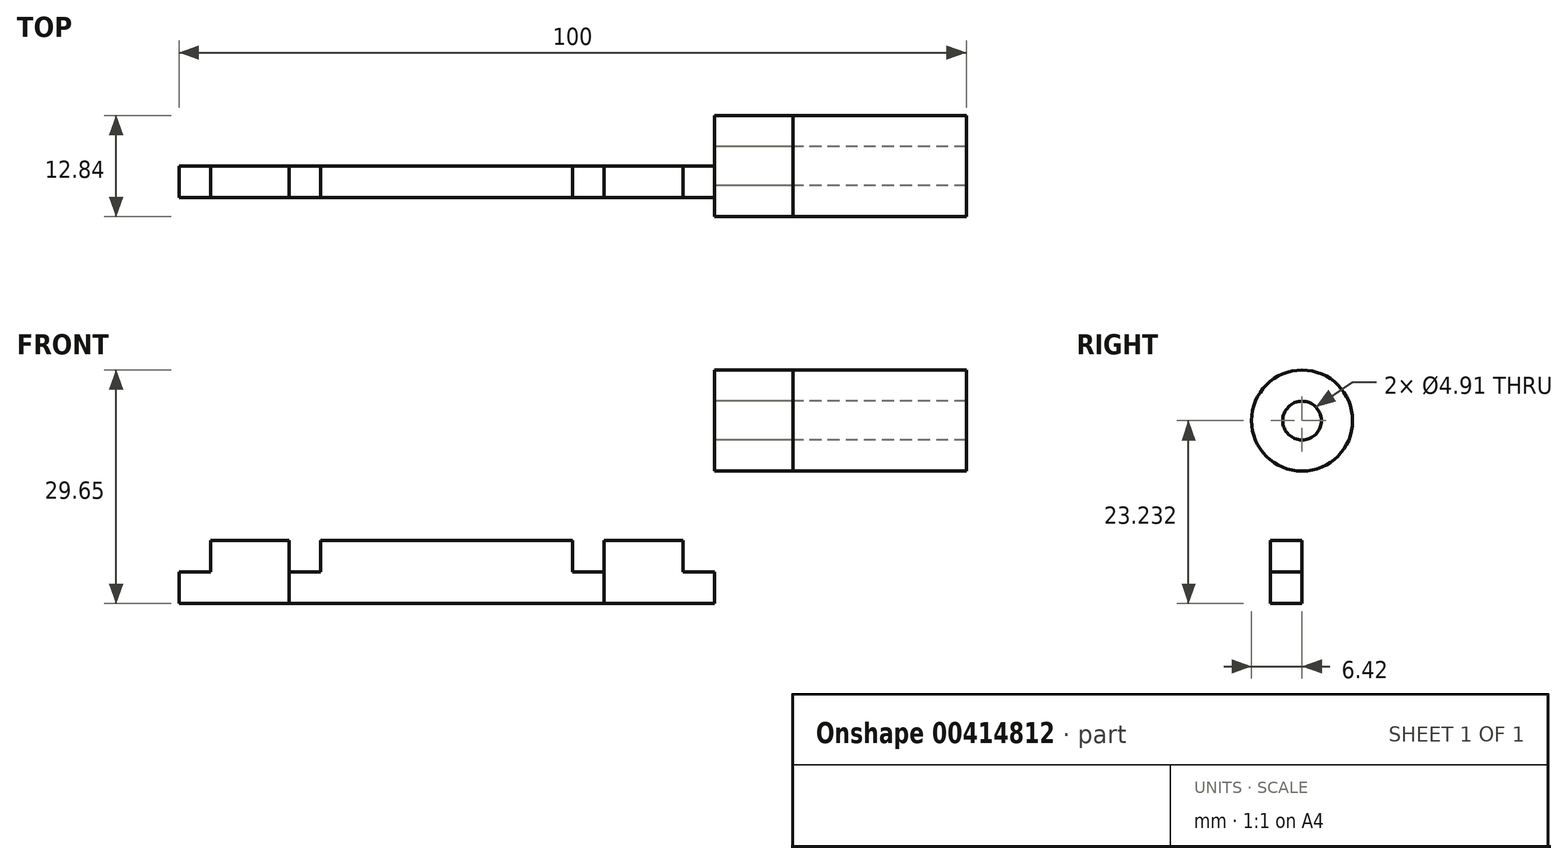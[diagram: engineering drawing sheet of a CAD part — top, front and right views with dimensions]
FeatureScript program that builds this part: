
annotation { "Feature Type Name" : "Feature", "Feature Type Description" : "" }
export const myFeature = defineFeature(function(context is Context, id is Id, definition is map)
    precondition{}
    {
        {
            var Q0;
            Q0=qCreatedBy(makeId("Front.planeOp"),FACE);
            var sketch = newSketch(context, id + "F0", { "sketchPlane" : qUnion([Q0])});
            skLineSegment(sketch, "E0", {"start": v(0, 0) * mm, "end": v(-68, 0) * mm});
            skLineSegment(sketch, "E1", {"start": v(-68, 0) * mm, "end": v(-68, 4) * mm});
            skLineSegment(sketch, "E2", {"start": v(-68, 4) * mm, "end": v(-64, 4) * mm});
            skLineSegment(sketch, "E3", {"start": v(-64, 4) * mm, "end": v(-64, 8) * mm});
            skLineSegment(sketch, "E4", {"start": v(-64, 8) * mm, "end": v(-54, 8) * mm});
            skLineSegment(sketch, "E5", {"start": v(-54, 8) * mm, "end": v(-54, 4) * mm});
            skLineSegment(sketch, "E6", {"start": v(-54, 4) * mm, "end": v(-50, 4) * mm});
            skLineSegment(sketch, "E7", {"start": v(-50, 4) * mm, "end": v(-50, 8) * mm});
            skLineSegment(sketch, "E8", {"start": v(-50, 8) * mm, "end": v(-18, 8) * mm});
            skLineSegment(sketch, "E9", {"start": v(-18, 8) * mm, "end": v(-18, 4) * mm});
            skLineSegment(sketch, "E10", {"start": v(-18, 4) * mm, "end": v(-14, 4) * mm});
            skLineSegment(sketch, "E11", {"start": v(-14, 4) * mm, "end": v(-14, 8) * mm});
            skLineSegment(sketch, "E12", {"start": v(-14, 8) * mm, "end": v(-4, 8) * mm});
            skLineSegment(sketch, "E13", {"start": v(-4, 8) * mm, "end": v(-4, 4) * mm});
            skLineSegment(sketch, "E14", {"start": v(-4, 4) * mm, "end": v(0, 4) * mm});
            skLineSegment(sketch, "E15", {"start": v(0, 4) * mm, "end": v(0, 0) * mm});
            skLineSegment(sketch, "E16", {"start": v(-54, 4) * mm, "end": v(-54, 0) * mm});
            skLineSegment(sketch, "E17", {"start": v(-14, 4) * mm, "end": v(-14, 0) * mm});
            skSolve(sketch);
        }
        {
            var Q0;
            Q0 = qSketchRegion(id + "F0", true);
            extrude(context, id + "F1", {"entities" : qUnion([Q0]), "depth" : 4 * mm});
        }
        {
            var Q0;
            Q0=makeQuery(id+"F0.imprint","IMPRINT",FACE,{"disambiguationData":[TD([[makeQuery(id+"F0.imprint","IMPRINT",EDGE,{"derivedFrom":sQuery(id+"F0.wireOp",EDGE,"E6")}),-1.0]])]});
            extrude(context, id + "F2", {"entities" : qUnion([Q0]), "depth" : 4 * mm});
        }
        {
            var Q0;
            Q0=qCreatedBy(makeId("Right.planeOp"),FACE);
            var sketch = newSketch(context, id + "F3", { "sketchPlane" : qUnion([Q0])});
            skCircle(sketch, "E18", {"center": v(0, 23.23) * mm, "radius": 2.46 * mm});
            skCircle(sketch, "E19", {"center": v(0, 23.23) * mm, "radius": 6.42 * mm});
            skSolve(sketch);
        }
        {
            var Q0;
            Q0 = qSketchRegion(id + "F3", true);
            extrude(context, id + "F4", {"entities" : qUnion([Q0]), "depth" : 32 * mm});
        }
        {
            var Q0;
            Q0=makeQuery(id+"F3.imprint","IMPRINT",FACE,{"disambiguationData":[TD([[makeQuery(id+"F3.imprint","IMPRINT",EDGE,{"derivedFrom":sQuery(id+"F3.wireOp",EDGE,"E18")}),-1.0]])]});
            extrude(context, id + "F5", {"entities" : qUnion([Q0]), "depth" : 10 * mm});
        }
    });
